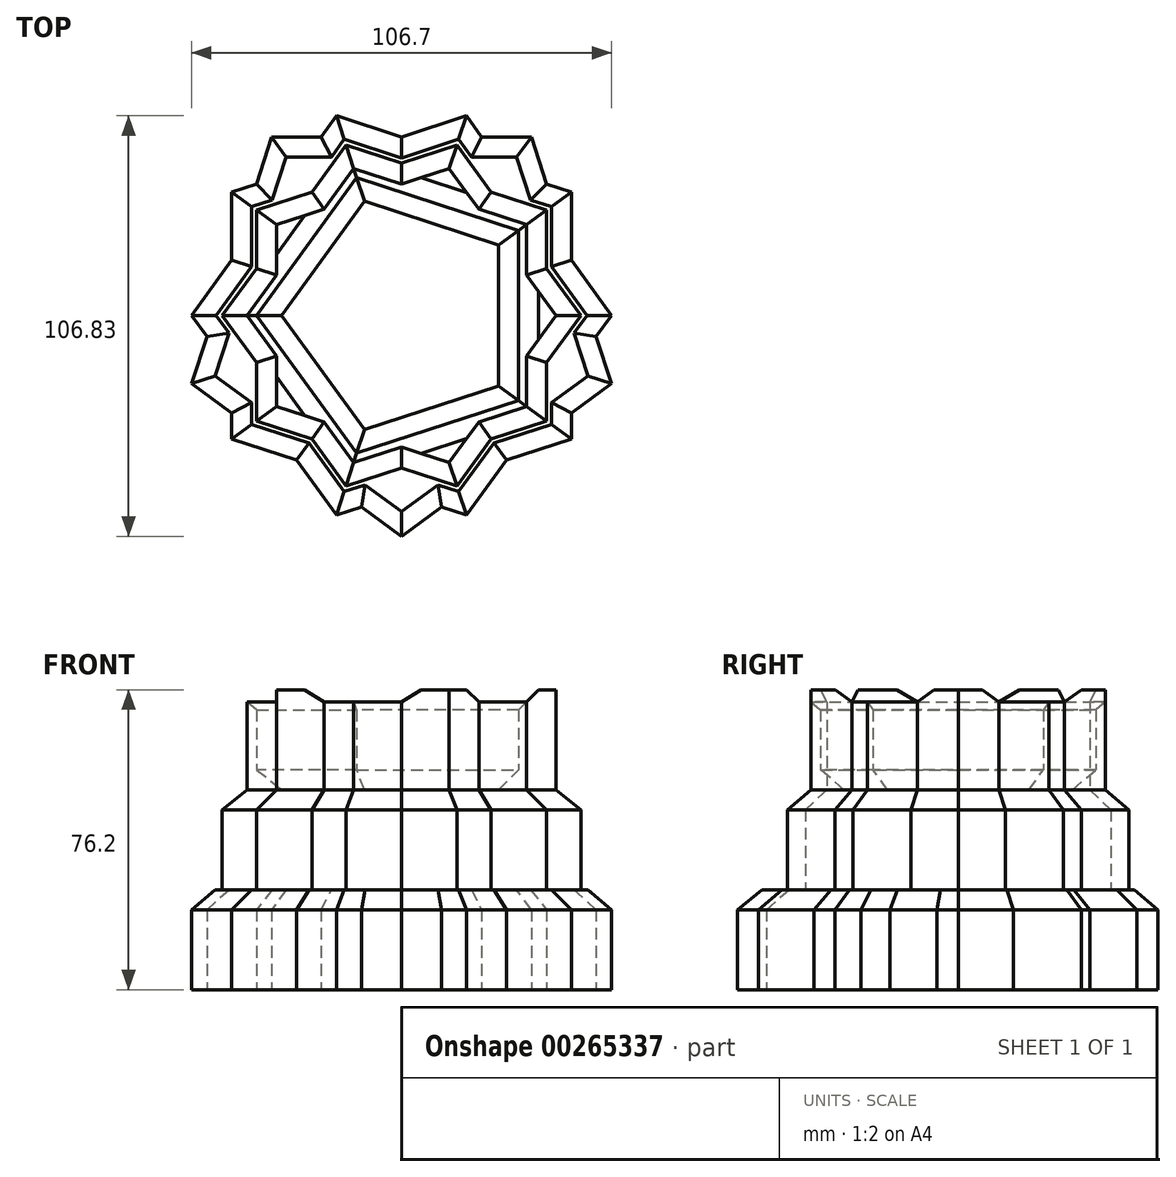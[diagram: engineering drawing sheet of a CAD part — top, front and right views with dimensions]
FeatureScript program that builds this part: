
annotation { "Feature Type Name" : "Feature", "Feature Type Description" : "" }
export const myFeature = defineFeature(function(context is Context, id is Id, definition is map)
    precondition{}
    {
        {
            var Q0;
            Q0=qCreatedBy(makeId("Top.planeOp"),FACE);
            var sketch = newSketch(context, id + "F0", { "sketchPlane" : qUnion([Q0])});
            skCircle(sketch, "E0.cCircle", {"center": v(0, 0) * mm, "radius": 43.16 * mm, "construction": true});
            skLineSegment(sketch, "E0.0", {"start": v(43.16, 31.36) * mm, "end": v(43.16, -31.36) * mm});
            skLineSegment(sketch, "E0.1", {"start": v(43.16, -31.36) * mm, "end": v(-16.48, -50.74) * mm});
            skLineSegment(sketch, "E0.2", {"start": v(-16.48, -50.74) * mm, "end": v(-53.35, 0) * mm});
            skLineSegment(sketch, "E0.3", {"start": v(-53.35, 0) * mm, "end": v(-16.48, 50.74) * mm});
            skLineSegment(sketch, "E0.4", {"start": v(-16.48, 50.74) * mm, "end": v(43.16, 31.36) * mm});
            skPoint(sketch, "E0.0.midPoint", {"position": v(43.16, 0) * mm});
            skLineSegment(sketch, "E1.0", {"start": v(-43.16, -31.36) * mm, "end": v(-43.16, 31.36) * mm});
            skLineSegment(sketch, "E1.1", {"start": v(-43.16, 31.36) * mm, "end": v(16.48, 50.74) * mm});
            skLineSegment(sketch, "E1.2", {"start": v(16.48, 50.74) * mm, "end": v(53.35, 0) * mm});
            skLineSegment(sketch, "E1.3", {"start": v(53.35, 0) * mm, "end": v(16.48, -50.74) * mm});
            skLineSegment(sketch, "E1.4", {"start": v(16.48, -50.74) * mm, "end": v(-43.16, -31.36) * mm});
            skPoint(sketch, "E1.0.midPoint", {"position": v(-43.16, 0) * mm});
            skCircle(sketch, "E2.cCircle", {"center": v(0, 0) * mm, "radius": 45.38 * mm, "construction": true});
            skLineSegment(sketch, "E2.0", {"start": v(-32.97, 45.38) * mm, "end": v(32.97, 45.38) * mm});
            skLineSegment(sketch, "E2.1", {"start": v(32.97, 45.38) * mm, "end": v(53.35, -17.33) * mm});
            skLineSegment(sketch, "E2.2", {"start": v(53.35, -17.33) * mm, "end": v(0, -56.1) * mm});
            skLineSegment(sketch, "E2.3", {"start": v(0, -56.1) * mm, "end": v(-53.35, -17.33) * mm});
            skLineSegment(sketch, "E2.4", {"start": v(-53.35, -17.33) * mm, "end": v(-32.97, 45.38) * mm});
            skPoint(sketch, "E2.0.midPoint", {"position": v(0, 45.38) * mm});
            skSolve(sketch);
        }
        {
            var Q0;
            Q0 = qSketchRegion(id + "F0", true);
            extrude(context, id + "F1", {"entities" : qUnion([Q0]), "depth" : 25.4 * mm});
        }
        {
            var Q0;
            Q0=makeQuery(id+"F1.opExtrude","CAP_FACE",FACE,{"disambiguationData":[OSD([sQuery(id+"F0.wireOp",EDGE,"E0.0"),sQuery(id+"F0.wireOp",EDGE,"E0.1"),sQuery(id+"F0.wireOp",EDGE,"E0.2"),sQuery(id+"F0.wireOp",EDGE,"E0.3"),sQuery(id+"F0.wireOp",EDGE,"E0.4"),sQuery(id+"F0.wireOp",EDGE,"E1.0"),sQuery(id+"F0.wireOp",EDGE,"E1.1"),sQuery(id+"F0.wireOp",EDGE,"E1.2"),sQuery(id+"F0.wireOp",EDGE,"E1.3"),sQuery(id+"F0.wireOp",EDGE,"E1.4"),sQuery(id+"F0.wireOp",EDGE,"E2.0"),sQuery(id+"F0.wireOp",EDGE,"E2.1"),sQuery(id+"F0.wireOp",EDGE,"E2.2"),sQuery(id+"F0.wireOp",EDGE,"E2.3"),sQuery(id+"F0.wireOp",EDGE,"E2.4")])],"isStart":false});
            chamfer(context, id + "F2", {"entities" : qUnion([Q0]), "width" : 5.08 * mm, "tangentPropagation" : true});
        }
        {
            var Q0;
            Q0=makeQuery(id+"F1.opExtrude","CAP_FACE",FACE,{"disambiguationData":[OSD([sQuery(id+"F0.wireOp",EDGE,"E0.0"),sQuery(id+"F0.wireOp",EDGE,"E0.1"),sQuery(id+"F0.wireOp",EDGE,"E0.2"),sQuery(id+"F0.wireOp",EDGE,"E0.3"),sQuery(id+"F0.wireOp",EDGE,"E0.4"),sQuery(id+"F0.wireOp",EDGE,"E1.0"),sQuery(id+"F0.wireOp",EDGE,"E1.1"),sQuery(id+"F0.wireOp",EDGE,"E1.2"),sQuery(id+"F0.wireOp",EDGE,"E1.3"),sQuery(id+"F0.wireOp",EDGE,"E1.4"),sQuery(id+"F0.wireOp",EDGE,"E2.0"),sQuery(id+"F0.wireOp",EDGE,"E2.1"),sQuery(id+"F0.wireOp",EDGE,"E2.2"),sQuery(id+"F0.wireOp",EDGE,"E2.3"),sQuery(id+"F0.wireOp",EDGE,"E2.4")])],"isStart":false});
            var sketch = newSketch(context, id + "F3", { "sketchPlane" : qUnion([Q0])});
            skCircle(sketch, "E3.cCircle", {"center": v(0, 0) * mm, "radius": 36.85 * mm, "construction": true});
            skLineSegment(sketch, "E3.0", {"start": v(36.85, 26.77) * mm, "end": v(36.85, -26.77) * mm});
            skLineSegment(sketch, "E3.1", {"start": v(36.85, -26.77) * mm, "end": v(-14.08, -43.32) * mm});
            skLineSegment(sketch, "E3.2", {"start": v(-14.08, -43.32) * mm, "end": v(-45.55, 0) * mm});
            skLineSegment(sketch, "E3.3", {"start": v(-45.55, 0) * mm, "end": v(-14.08, 43.32) * mm});
            skLineSegment(sketch, "E3.4", {"start": v(-14.08, 43.32) * mm, "end": v(36.85, 26.77) * mm});
            skPoint(sketch, "E3.0.midPoint", {"position": v(36.85, 0) * mm});
            skLineSegment(sketch, "E4.0", {"start": v(-36.85, -26.77) * mm, "end": v(-36.85, 26.77) * mm});
            skLineSegment(sketch, "E4.1", {"start": v(-36.85, 26.77) * mm, "end": v(14.08, 43.32) * mm});
            skLineSegment(sketch, "E4.2", {"start": v(14.08, 43.32) * mm, "end": v(45.55, 0) * mm});
            skLineSegment(sketch, "E4.3", {"start": v(45.55, 0) * mm, "end": v(14.08, -43.32) * mm});
            skLineSegment(sketch, "E4.4", {"start": v(14.08, -43.32) * mm, "end": v(-36.85, -26.77) * mm});
            skPoint(sketch, "E4.0.midPoint", {"position": v(-36.85, 0) * mm});
            skSolve(sketch);
        }
        {
            var Q0;
            Q0 = qSketchRegion(id + "F3", true);
            extrude(context, id + "F4", {"entities" : qUnion([Q0]), "operationType" : NewBodyOperationType.ADD, "depth" : 25.4 * mm});
        }
        {
            var Q0;
            Q0=makeQuery(id+"F4.opExtrude","CAP_FACE",FACE,{"disambiguationData":[OSD([sQuery(id+"F3.wireOp",EDGE,"E3.0"),sQuery(id+"F3.wireOp",EDGE,"E3.1"),sQuery(id+"F3.wireOp",EDGE,"E3.2"),sQuery(id+"F3.wireOp",EDGE,"E3.3"),sQuery(id+"F3.wireOp",EDGE,"E3.4"),sQuery(id+"F3.wireOp",EDGE,"E4.0"),sQuery(id+"F3.wireOp",EDGE,"E4.1"),sQuery(id+"F3.wireOp",EDGE,"E4.2"),sQuery(id+"F3.wireOp",EDGE,"E4.3"),sQuery(id+"F3.wireOp",EDGE,"E4.4")])],"isStart":false});
            chamfer(context, id + "F5", {"entities" : qUnion([Q0]), "width" : 5.08 * mm, "tangentPropagation" : true});
        }
        {
            var Q0;
            Q0=makeQuery(id+"F4.opExtrude","CAP_FACE",FACE,{"disambiguationData":[OSD([sQuery(id+"F3.wireOp",EDGE,"E3.0"),sQuery(id+"F3.wireOp",EDGE,"E3.1"),sQuery(id+"F3.wireOp",EDGE,"E3.2"),sQuery(id+"F3.wireOp",EDGE,"E3.3"),sQuery(id+"F3.wireOp",EDGE,"E3.4"),sQuery(id+"F3.wireOp",EDGE,"E4.0"),sQuery(id+"F3.wireOp",EDGE,"E4.1"),sQuery(id+"F3.wireOp",EDGE,"E4.2"),sQuery(id+"F3.wireOp",EDGE,"E4.3"),sQuery(id+"F3.wireOp",EDGE,"E4.4")])],"isStart":false});
            var sketch = newSketch(context, id + "F6", { "sketchPlane" : qUnion([Q0])});
            skCircle(sketch, "E5.cCircle", {"center": v(0, 0) * mm, "radius": 29.76 * mm, "construction": true});
            skLineSegment(sketch, "E5.0", {"start": v(29.76, 21.62) * mm, "end": v(29.76, -21.62) * mm});
            skLineSegment(sketch, "E5.1", {"start": v(29.76, -21.62) * mm, "end": v(-11.37, -34.98) * mm});
            skLineSegment(sketch, "E5.2", {"start": v(-11.37, -34.98) * mm, "end": v(-36.78, 0) * mm});
            skLineSegment(sketch, "E5.3", {"start": v(-36.78, 0) * mm, "end": v(-11.37, 34.98) * mm});
            skLineSegment(sketch, "E5.4", {"start": v(-11.37, 34.98) * mm, "end": v(29.76, 21.62) * mm});
            skPoint(sketch, "E5.0.midPoint", {"position": v(29.76, 0) * mm});
            skSolve(sketch);
        }
        {
            var Q0;
            Q0=makeQuery(id+"F6.imprint","IMPRINT",FACE,{"disambiguationData":[TD([[makeQuery(id+"F6.imprint","IMPRINT",EDGE,{"derivedFrom":sQuery(id+"F6.wireOp",EDGE,"E5.0")}),1.0]])]});
            extrude(context, id + "F7", {"entities" : qUnion([Q0]), "operationType" : NewBodyOperationType.ADD, "depth" : 25.4 * mm});
        }
        {
            var Q0;
            Q0=makeQuery(id+"F4.opExtrude","CAP_FACE",FACE,{"disambiguationData":[OSD([sQuery(id+"F3.wireOp",EDGE,"E3.0"),sQuery(id+"F3.wireOp",EDGE,"E3.1"),sQuery(id+"F3.wireOp",EDGE,"E3.2"),sQuery(id+"F3.wireOp",EDGE,"E3.3"),sQuery(id+"F3.wireOp",EDGE,"E3.4"),sQuery(id+"F3.wireOp",EDGE,"E4.0"),sQuery(id+"F3.wireOp",EDGE,"E4.1"),sQuery(id+"F3.wireOp",EDGE,"E4.2"),sQuery(id+"F3.wireOp",EDGE,"E4.3"),sQuery(id+"F3.wireOp",EDGE,"E4.4")])],"isStart":false});
            chamfer(context, id + "F8", {"entities" : qUnion([Q0]), "width" : 5.08 * mm, "tangentPropagation" : true});
        }
        {
            var Q0;
            Q0=makeQuery(id+"F7.opExtrude","CAP_EDGE",EDGE,{"disambiguationData":[OSD([sQuery(id+"F6.wireOp",EDGE,"E5.3")])],"isStart":false});
            var Q1;
            Q1=makeQuery(id+"F7.opExtrude","CAP_EDGE",EDGE,{"disambiguationData":[OSD([sQuery(id+"F6.wireOp",EDGE,"E5.4")])],"isStart":false});
            var Q2;
            Q2=makeQuery(id+"F7.opExtrude","CAP_EDGE",EDGE,{"disambiguationData":[OSD([sQuery(id+"F6.wireOp",EDGE,"E5.0")])],"isStart":false});
            var Q3;
            Q3=makeQuery(id+"F7.opExtrude","CAP_EDGE",EDGE,{"disambiguationData":[OSD([sQuery(id+"F6.wireOp",EDGE,"E5.1")])],"isStart":false});
            var Q4;
            Q4=makeQuery(id+"F7.opExtrude","CAP_EDGE",EDGE,{"disambiguationData":[OSD([sQuery(id+"F6.wireOp",EDGE,"E5.2")])],"isStart":false});
            chamfer(context, id + "F9", {"entities" : qUnion([Q0, Q1, Q2, Q3, Q4]), "width" : 5.08 * mm, "tangentPropagation" : true});
        }
    });
